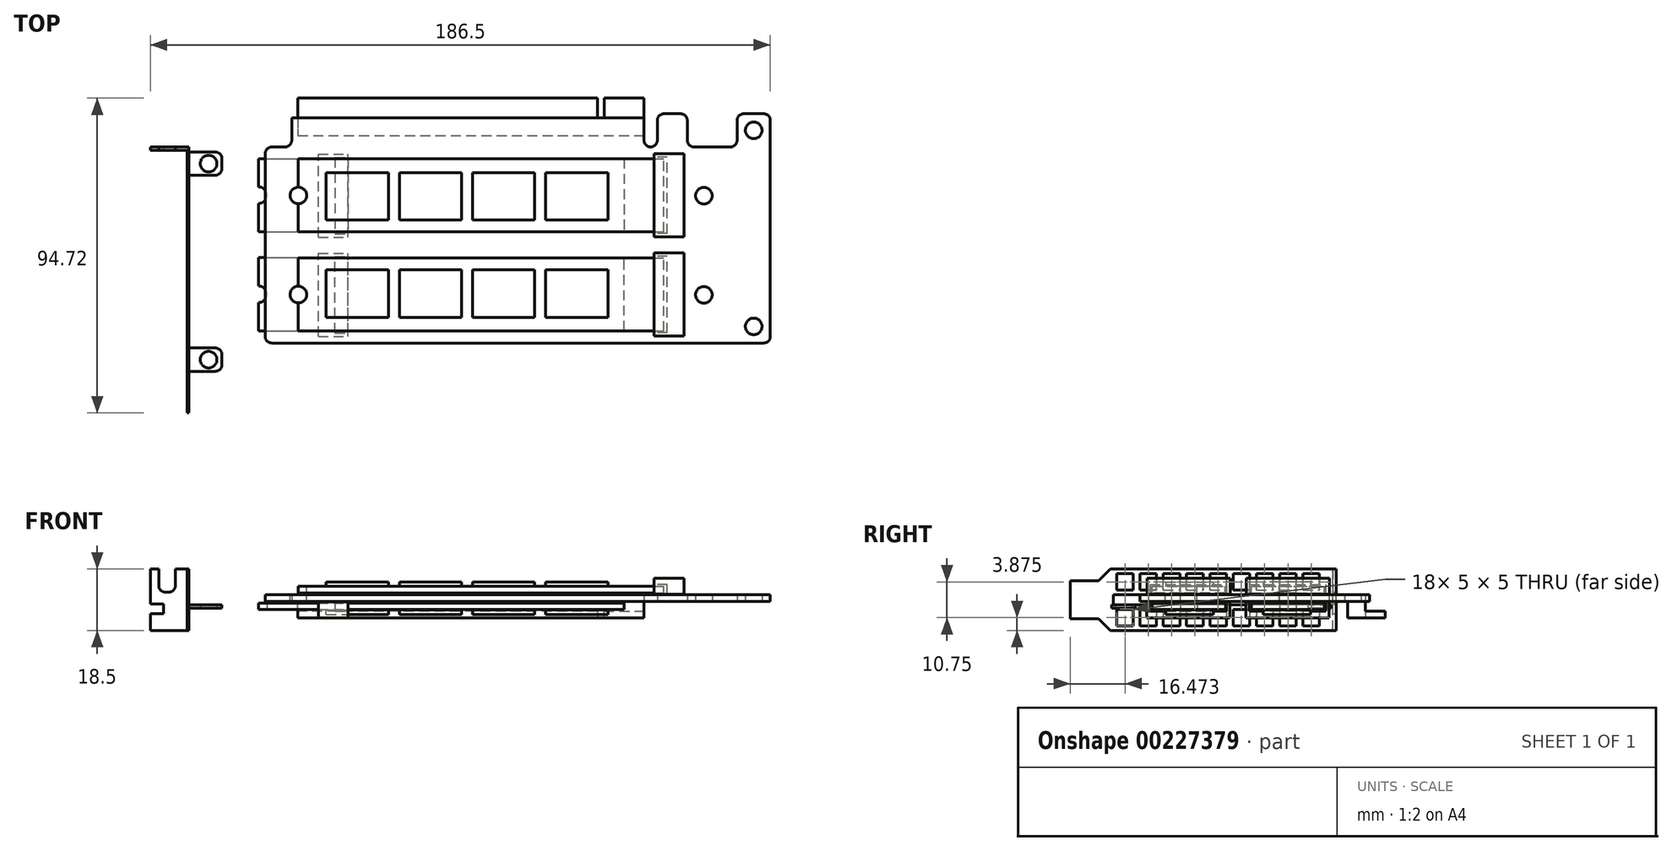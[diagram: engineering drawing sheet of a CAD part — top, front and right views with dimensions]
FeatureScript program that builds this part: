
annotation { "Feature Type Name" : "Feature", "Feature Type Description" : "" }
export const myFeature = defineFeature(function(context is Context, id is Id, definition is map)
    precondition{}
    {
        {
            var Q0;
            Q0=qCreatedBy(makeId("Top.planeOp"),FACE);
            var sketch = newSketch(context, id + "F0", { "sketchPlane" : qUnion([Q0])});
            skLineSegment(sketch, "E0.top", {"start": v(76, 34.5) * mm, "end": v(-76, 34.5) * mm});
            skLineSegment(sketch, "E0.right", {"start": v(-76, -34.5) * mm, "end": v(-76, 34.5) * mm});
            skPoint(sketch, "E0.middle", {"position": v(0, 0) * mm});
            skLineSegment(sketch, "E1", {"start": v(-76, -34.5) * mm, "end": v(-66, -34.5) * mm});
            skLineSegment(sketch, "E2", {"start": v(-66, -34.5) * mm, "end": v(-66, -24.5) * mm});
            skLineSegment(sketch, "E3", {"start": v(-66, -24.5) * mm, "end": v(-51, -24.5) * mm});
            skLineSegment(sketch, "E4", {"start": v(-51, -24.5) * mm, "end": v(-51, -34.5) * mm});
            skLineSegment(sketch, "E5", {"start": v(-51, -34.5) * mm, "end": v(-42, -34.5) * mm});
            skLineSegment(sketch, "E6", {"start": v(-42, -34.5) * mm, "end": v(-42, -24.5) * mm});
            skLineSegment(sketch, "E7", {"start": v(-42, -24.5) * mm, "end": v(-38, -24.5) * mm});
            skLineSegment(sketch, "E8", {"start": v(-38, -24.5) * mm, "end": v(-38, -39.95) * mm});
            skLineSegment(sketch, "E9", {"start": v(-38, -39.95) * mm, "end": v(-26, -39.95) * mm});
            skLineSegment(sketch, "E10", {"start": v(-26, -39.95) * mm, "end": v(-26, -29.95) * mm});
            skLineSegment(sketch, "E11", {"start": v(-26, -29.95) * mm, "end": v(-24, -29.95) * mm});
            skLineSegment(sketch, "E12", {"start": v(-24, -29.95) * mm, "end": v(-24, -39.95) * mm});
            skLineSegment(sketch, "E13", {"start": v(-24, -39.95) * mm, "end": v(68, -39.95) * mm});
            skLineSegment(sketch, "E14", {"start": v(68, -39.95) * mm, "end": v(68, -24.5) * mm});
            skLineSegment(sketch, "E15", {"start": v(76, 34.5) * mm, "end": v(76, -24.5) * mm});
            skLineSegment(sketch, "E16", {"start": v(-76, -34.5) * mm, "end": v(-66, -24.5) * mm, "construction": true});
            skCircle(sketch, "E17", {"center": v(-71, -29.5) * mm, "radius": 2.5 * mm});
            skLineSegment(sketch, "E18", {"start": v(-76, 0) * mm, "end": v(0, 0) * mm, "construction": true});
            skCircle(sketch, "E19.MirrorC", {"center": v(-71, 29.5) * mm, "radius": 2.5 * mm});
            skLineSegment(sketch, "E20", {"start": v(68, -24.5) * mm, "end": v(76, -24.5) * mm});
            skSolve(sketch);
        }
        {
            var Q0;
            Q0 = qSketchRegion(id + "F0", true);
            extrude(context, id + "F1", {"entities" : qUnion([Q0]), "depth" : 2 * mm});
        }
        {
            var Q0;
            Q0=makeQuery(id+"F1.opExtrude","CAP_FACE",FACE,{"disambiguationData":[OSD([sQuery(id+"F0.wireOp",EDGE,"E0.top"),sQuery(id+"F0.wireOp",EDGE,"E0.right"),sQuery(id+"F0.wireOp",EDGE,"E1"),sQuery(id+"F0.wireOp",EDGE,"E2"),sQuery(id+"F0.wireOp",EDGE,"E3"),sQuery(id+"F0.wireOp",EDGE,"E4"),sQuery(id+"F0.wireOp",EDGE,"E5"),sQuery(id+"F0.wireOp",EDGE,"E6"),sQuery(id+"F0.wireOp",EDGE,"E7"),sQuery(id+"F0.wireOp",EDGE,"E8"),sQuery(id+"F0.wireOp",EDGE,"E9"),sQuery(id+"F0.wireOp",EDGE,"E10"),sQuery(id+"F0.wireOp",EDGE,"E11"),sQuery(id+"F0.wireOp",EDGE,"E12"),sQuery(id+"F0.wireOp",EDGE,"E13"),sQuery(id+"F0.wireOp",EDGE,"E14"),sQuery(id+"F0.wireOp",EDGE,"E15"),sQuery(id+"F0.wireOp",EDGE,"E17"),sQuery(id+"F0.wireOp",EDGE,"E19.MirrorC"),sQuery(id+"F0.wireOp",EDGE,"E20")])],"isStart":false});
            var sketch = newSketch(context, id + "F2", { "sketchPlane" : qUnion([Q0])});
            skLineSegment(sketch, "E21.bottom", {"start": v(-50, 2.58) * mm, "end": v(-41, 2.58) * mm});
            skLineSegment(sketch, "E21.top", {"start": v(-50, -22.42) * mm, "end": v(-41, -22.42) * mm});
            skLineSegment(sketch, "E21.left", {"start": v(-50, 2.58) * mm, "end": v(-50, -22.42) * mm});
            skLineSegment(sketch, "E21.right", {"start": v(-41, 2.58) * mm, "end": v(-41, -22.42) * mm});
            skLineSegment(sketch, "E22", {"start": v(-66, -24.5) * mm, "end": v(-66, 34.5) * mm, "construction": true});
            skLineSegment(sketch, "E23", {"start": v(-66, 5) * mm, "end": v(-44.12, 5) * mm, "construction": true});
            skLineSegment(sketch, "E24.MirrorCS", {"start": v(-41, 7.42) * mm, "end": v(-41, 32.42) * mm});
            skLineSegment(sketch, "E25.MirrorCS", {"start": v(-50, 7.42) * mm, "end": v(-41, 7.42) * mm});
            skLineSegment(sketch, "E26.MirrorCS", {"start": v(-50, 7.42) * mm, "end": v(-50, 32.42) * mm});
            skLineSegment(sketch, "E27.MirrorCS", {"start": v(-50, 32.42) * mm, "end": v(-41, 32.42) * mm});
            skLineSegment(sketch, "E28", {"start": v(-50, 32.42) * mm, "end": v(-66, 32.42) * mm, "construction": true});
            skLineSegment(sketch, "E29.bottom", {"start": v(-36.45, -34.95) * mm, "end": v(-27.66, -34.95) * mm});
            skLineSegment(sketch, "E29.top", {"start": v(-36.45, -39.95) * mm, "end": v(-27.66, -39.95) * mm});
            skLineSegment(sketch, "E29.left", {"start": v(-36.45, -34.95) * mm, "end": v(-36.45, -39.95) * mm});
            skLineSegment(sketch, "E29.right", {"start": v(-27.66, -34.95) * mm, "end": v(-27.66, -39.95) * mm});
            skLineSegment(sketch, "E30.bottom", {"start": v(-22.05, -34.95) * mm, "end": v(65.79, -34.95) * mm});
            skLineSegment(sketch, "E30.top", {"start": v(-22.05, -39.95) * mm, "end": v(65.79, -39.95) * mm});
            skLineSegment(sketch, "E30.left", {"start": v(-22.05, -34.95) * mm, "end": v(-22.05, -39.95) * mm});
            skLineSegment(sketch, "E30.right", {"start": v(65.79, -34.95) * mm, "end": v(65.79, -39.95) * mm});
            skSolve(sketch);
        }
        {
            var Q0;
            Q0=makeQuery(id+"F2.imprint","IMPRINT",FACE,{"disambiguationData":[TD([[makeQuery(id+"F2.imprint","IMPRINT",EDGE,{"derivedFrom":sQuery(id+"F2.wireOp",EDGE,"E21.bottom")}),-1.0]])]});
            var Q1;
            Q1=makeQuery(id+"F2.imprint","IMPRINT",FACE,{"disambiguationData":[TD([[makeQuery(id+"F2.imprint","IMPRINT",EDGE,{"derivedFrom":sQuery(id+"F2.wireOp",EDGE,"E24.MirrorCS")}),1.0]])]});
            extrude(context, id + "F3", {"entities" : qUnion([Q0, Q1]), "operationType" : NewBodyOperationType.ADD, "depth" : 5 * mm});
        }
        {
            var Q0;
            Q0=makeQuery(id+"F3.opExtrude","SWEPT_FACE",FACE,{"disambiguationData":[OSD([sQuery(id+"F2.wireOp",EDGE,"E24.MirrorCS")])]});
            var sketch = newSketch(context, id + "F4", { "sketchPlane" : qUnion([Q0])});
            skLineSegment(sketch, "E31.bottom", {"start": v(31.42, 2) * mm, "end": v(8.42, 2) * mm});
            skLineSegment(sketch, "E31.top", {"start": v(31.42, 5) * mm, "end": v(8.42, 5) * mm});
            skLineSegment(sketch, "E31.left", {"start": v(31.42, 2) * mm, "end": v(31.42, 5) * mm});
            skLineSegment(sketch, "E31.right", {"start": v(8.42, 2) * mm, "end": v(8.42, 5) * mm});
            skLineSegment(sketch, "E32", {"start": v(31.42, 3.5) * mm, "end": v(32.42, 3.5) * mm, "construction": true});
            skSolve(sketch);
        }
        {
            var Q0;
            Q0 = qSketchRegion(id + "F4", true);
            extrude(context, id + "F5", {"entities" : qUnion([Q0]), "operationType" : NewBodyOperationType.REMOVE, "oppositeDirection" : true, "depth" : 4 * mm});
        }
        {
            var Q0;
            Q0=makeQuery(id+"F3.opExtrude","SWEPT_FACE",FACE,{"disambiguationData":[OSD([sQuery(id+"F2.wireOp",EDGE,"E21.right")])]});
            var sketch = newSketch(context, id + "F6", { "sketchPlane" : qUnion([Q0])});
            skLineSegment(sketch, "E33.0", {"start": v(31.42, 5) * mm, "end": v(8.42, 5) * mm, "construction": true});
            skLineSegment(sketch, "E34.0", {"start": v(8.42, 2) * mm, "end": v(8.42, 5) * mm, "construction": true});
            skLineSegment(sketch, "E35", {"start": v(2.58, 4.5) * mm, "end": v(1.58, 4.5) * mm, "construction": true});
            skLineSegment(sketch, "E36.bottom", {"start": v(1.58, 2) * mm, "end": v(-21.42, 2) * mm});
            skLineSegment(sketch, "E36.top", {"start": v(1.58, 5) * mm, "end": v(-21.42, 5) * mm});
            skLineSegment(sketch, "E36.left", {"start": v(1.58, 2) * mm, "end": v(1.58, 5) * mm});
            skLineSegment(sketch, "E36.right", {"start": v(-21.42, 2) * mm, "end": v(-21.42, 5) * mm});
            skSolve(sketch);
        }
        {
            var Q0;
            Q0 = qSketchRegion(id + "F6", true);
            extrude(context, id + "F7", {"entities" : qUnion([Q0]), "operationType" : NewBodyOperationType.REMOVE, "oppositeDirection" : true, "depth" : 4 * mm});
        }
        {
            var Q0;
            Q0=makeQuery(id+"F7.boolean.opBoolean","COPY",FACE,{"derivedFrom":makeQuery(id+"F7.opExtrude","CAP_FACE",FACE,{"disambiguationData":[OSD([sQuery(id+"F6.wireOp",EDGE,"E36.bottom"),sQuery(id+"F6.wireOp",EDGE,"E36.top"),sQuery(id+"F6.wireOp",EDGE,"E36.left"),sQuery(id+"F6.wireOp",EDGE,"E36.right")])],"isStart":false})});
            cPlane(context, id + "F8", {"entities" : qUnion([Q0]), "cplaneType" : CPlaneType.OFFSET, "offset" : 1 * mm, "width" : 150 * mm, "height" : 150 * mm});
        }
        {
            var Q0;
            Q0=qCreatedBy(id+"F8.planeOp",FACE);
            var sketch = newSketch(context, id + "F9", { "sketchPlane" : qUnion([Q0])});
            skLineSegment(sketch, "E37.0", {"start": v(1.58, 5) * mm, "end": v(-21.42, 5) * mm, "construction": true});
            skLineSegment(sketch, "E37.1", {"start": v(1.58, 2) * mm, "end": v(1.58, 5) * mm, "construction": true});
            skLineSegment(sketch, "E37.2", {"start": v(-21.42, 2) * mm, "end": v(-21.42, 5) * mm, "construction": true});
            skLineSegment(sketch, "E37.3", {"start": v(8.42, 2) * mm, "end": v(31.42, 2) * mm, "construction": true});
            skLineSegment(sketch, "E37.4", {"start": v(8.42, 2) * mm, "end": v(8.42, 5) * mm, "construction": true});
            skLineSegment(sketch, "E37.5", {"start": v(31.42, 2) * mm, "end": v(31.42, 5) * mm, "construction": true});
            skLineSegment(sketch, "E37.6", {"start": v(31.42, 5) * mm, "end": v(8.42, 5) * mm, "construction": true});
            skLineSegment(sketch, "E37.7", {"start": v(1.58, 2) * mm, "end": v(-21.42, 2) * mm, "construction": true});
            skPoint(sketch, "E37.8", {"position": v(8.42, 3.5) * mm});
            skLineSegment(sketch, "E38.0", {"start": v(8.92, 2.5) * mm, "end": v(30.92, 2.5) * mm});
            skLineSegment(sketch, "E38.1", {"start": v(8.92, 2.5) * mm, "end": v(8.92, 4.5) * mm});
            skLineSegment(sketch, "E38.2", {"start": v(30.92, 4.5) * mm, "end": v(8.92, 4.5) * mm});
            skLineSegment(sketch, "E38.3", {"start": v(30.92, 2.5) * mm, "end": v(30.92, 4.5) * mm});
            skLineSegment(sketch, "E39.0", {"start": v(1.08, 4.5) * mm, "end": v(-20.92, 4.5) * mm});
            skLineSegment(sketch, "E39.1", {"start": v(1.08, 2.5) * mm, "end": v(1.08, 4.5) * mm});
            skLineSegment(sketch, "E39.2", {"start": v(1.08, 2.5) * mm, "end": v(-20.92, 2.5) * mm});
            skLineSegment(sketch, "E39.3", {"start": v(-20.92, 2.5) * mm, "end": v(-20.92, 4.5) * mm});
            skSolve(sketch);
        }
        {
            var Q0;
            Q0 = qSketchRegion(id + "F9", true);
            extrude(context, id + "F10", {"entities" : qUnion([Q0]), "depth" : 110 * mm});
        }
        {
            var Q0;
            Q0=makeQuery(id+"F1.opExtrude","CAP_FACE",FACE,{"disambiguationData":[OSD([sQuery(id+"F0.wireOp",EDGE,"E0.top"),sQuery(id+"F0.wireOp",EDGE,"E0.right"),sQuery(id+"F0.wireOp",EDGE,"E1"),sQuery(id+"F0.wireOp",EDGE,"E2"),sQuery(id+"F0.wireOp",EDGE,"E3"),sQuery(id+"F0.wireOp",EDGE,"E4"),sQuery(id+"F0.wireOp",EDGE,"E5"),sQuery(id+"F0.wireOp",EDGE,"E6"),sQuery(id+"F0.wireOp",EDGE,"E7"),sQuery(id+"F0.wireOp",EDGE,"E8"),sQuery(id+"F0.wireOp",EDGE,"E9"),sQuery(id+"F0.wireOp",EDGE,"E10"),sQuery(id+"F0.wireOp",EDGE,"E11"),sQuery(id+"F0.wireOp",EDGE,"E12"),sQuery(id+"F0.wireOp",EDGE,"E13"),sQuery(id+"F0.wireOp",EDGE,"E14"),sQuery(id+"F0.wireOp",EDGE,"E15"),sQuery(id+"F0.wireOp",EDGE,"E17"),sQuery(id+"F0.wireOp",EDGE,"E19.MirrorC"),sQuery(id+"F0.wireOp",EDGE,"E20")])],"isStart":true});
            var sketch = newSketch(context, id + "F11", { "sketchPlane" : qUnion([Q0])});
            skLineSegment(sketch, "E40", {"start": v(60, -34.5) * mm, "end": v(60, -32.5) * mm, "construction": true});
            skLineSegment(sketch, "E41", {"start": v(60, -32.5) * mm, "end": v(76, -32.5) * mm, "construction": true});
            skLineSegment(sketch, "E42.bottom", {"start": v(60, -32.5) * mm, "end": v(51, -32.5) * mm});
            skLineSegment(sketch, "E42.top", {"start": v(60, -7.5) * mm, "end": v(51, -7.5) * mm});
            skLineSegment(sketch, "E42.left", {"start": v(60, -32.5) * mm, "end": v(60, -7.5) * mm});
            skLineSegment(sketch, "E42.right", {"start": v(51, -32.5) * mm, "end": v(51, -7.5) * mm});
            skLineSegment(sketch, "E43", {"start": v(60, -7.5) * mm, "end": v(60, -2.67) * mm, "construction": true});
            skLineSegment(sketch, "E44.bottom", {"start": v(60, -2.67) * mm, "end": v(51, -2.67) * mm});
            skLineSegment(sketch, "E44.top", {"start": v(60, 22.33) * mm, "end": v(51, 22.33) * mm});
            skLineSegment(sketch, "E44.left", {"start": v(60, -2.67) * mm, "end": v(60, 22.33) * mm});
            skLineSegment(sketch, "E44.right", {"start": v(51, -2.67) * mm, "end": v(51, 22.33) * mm});
            skPoint(sketch, "E45.0", {"position": v(65.79, 37.45) * mm});
            skLineSegment(sketch, "E46.0", {"start": v(65.79, 34.95) * mm, "end": v(65.79, 39.95) * mm});
            skLineSegment(sketch, "E47.0", {"start": v(-22.05, 34.95) * mm, "end": v(65.79, 34.95) * mm});
            skLineSegment(sketch, "E48.0", {"start": v(-22.05, 39.95) * mm, "end": v(65.79, 39.95) * mm});
            skPoint(sketch, "E49.0", {"position": v(-22.05, 37.45) * mm});
            skLineSegment(sketch, "E50.0", {"start": v(-22.05, 34.95) * mm, "end": v(-22.05, 39.95) * mm});
            skLineSegment(sketch, "E51.0", {"start": v(-27.66, 34.95) * mm, "end": v(-27.66, 39.95) * mm});
            skLineSegment(sketch, "E52.0", {"start": v(-36.45, 34.95) * mm, "end": v(-27.66, 34.95) * mm});
            skLineSegment(sketch, "E53.0", {"start": v(-36.45, 34.95) * mm, "end": v(-36.45, 39.95) * mm});
            skLineSegment(sketch, "E54.0", {"start": v(-36.45, 39.95) * mm, "end": v(-27.66, 39.95) * mm});
            skSolve(sketch);
        }
        {
            var Q0;
            Q0=makeQuery(id+"F11.imprint","IMPRINT",FACE,{"disambiguationData":[TD([[makeQuery(id+"F11.imprint","IMPRINT",EDGE,{"derivedFrom":sQuery(id+"F11.wireOp",EDGE,"E42.bottom")}),-1.0]])]});
            var Q1;
            Q1=makeQuery(id+"F11.imprint","IMPRINT",FACE,{"disambiguationData":[TD([[makeQuery(id+"F11.imprint","IMPRINT",EDGE,{"derivedFrom":sQuery(id+"F11.wireOp",EDGE,"E44.bottom")}),-1.0]])]});
            extrude(context, id + "F12", {"entities" : qUnion([Q0, Q1]), "operationType" : NewBodyOperationType.ADD, "depth" : 5 * mm});
        }
        {
            var Q0;
            Q0=makeQuery(id+"F12.opExtrude","SWEPT_FACE",FACE,{"disambiguationData":[OSD([sQuery(id+"F11.wireOp",EDGE,"E42.right")])]});
            var sketch = newSketch(context, id + "F13", { "sketchPlane" : qUnion([Q0])});
            skPoint(sketch, "E55.0", {"position": v(-2.67, -5) * mm});
            skLineSegment(sketch, "E56", {"start": v(-7.5, -5) * mm, "end": v(-2.67, -5) * mm, "construction": true});
            skLineSegment(sketch, "E57", {"start": v(-5.09, -5) * mm, "end": v(-5.09, 0) * mm, "construction": true});
            skLineSegment(sketch, "E58.bottom", {"start": v(-31.5, 0) * mm, "end": v(-8.5, 0) * mm});
            skLineSegment(sketch, "E58.top", {"start": v(-31.5, -3) * mm, "end": v(-8.5, -3) * mm});
            skLineSegment(sketch, "E58.left", {"start": v(-31.5, 0) * mm, "end": v(-31.5, -3) * mm});
            skLineSegment(sketch, "E58.right", {"start": v(-8.5, 0) * mm, "end": v(-8.5, -3) * mm});
            skLineSegment(sketch, "E59", {"start": v(-31.5, -1.5) * mm, "end": v(-32.5, -1.5) * mm, "construction": true});
            skLineSegment(sketch, "E60", {"start": v(-8.5, -1.5) * mm, "end": v(-7.5, -1.5) * mm, "construction": true});
            skLineSegment(sketch, "E61.MirrorCS", {"start": v(-1.67, 0) * mm, "end": v(-1.67, -3) * mm});
            skLineSegment(sketch, "E62.MirrorCS", {"start": v(21.33, -3) * mm, "end": v(-1.67, -3) * mm});
            skLineSegment(sketch, "E63.MirrorCS", {"start": v(21.33, 0) * mm, "end": v(-1.67, 0) * mm});
            skLineSegment(sketch, "E64.MirrorCS", {"start": v(21.33, 0) * mm, "end": v(21.33, -3) * mm});
            skSolve(sketch);
        }
        {
            var Q0;
            Q0 = qSketchRegion(id + "F13", true);
            extrude(context, id + "F14", {"entities" : qUnion([Q0]), "operationType" : NewBodyOperationType.REMOVE, "oppositeDirection" : true, "depth" : 4 * mm});
        }
        {
            var Q0;
            Q0=makeQuery(id+"F14.boolean.opBoolean","COPY",FACE,{"derivedFrom":makeQuery(id+"F14.opExtrude","CAP_FACE",FACE,{"disambiguationData":[OSD([sQuery(id+"F13.wireOp",EDGE,"E58.bottom"),sQuery(id+"F13.wireOp",EDGE,"E58.top"),sQuery(id+"F13.wireOp",EDGE,"E58.left"),sQuery(id+"F13.wireOp",EDGE,"E58.right")])],"isStart":false})});
            cPlane(context, id + "F15", {"entities" : qUnion([Q0]), "cplaneType" : CPlaneType.OFFSET, "offset" : 1 * mm, "width" : 150 * mm, "height" : 150 * mm});
        }
        {
            var Q0;
            Q0=qCreatedBy(id+"F15.planeOp",FACE);
            var sketch = newSketch(context, id + "F16", { "sketchPlane" : qUnion([Q0])});
            skLineSegment(sketch, "E65.0.0", {"start": v(-8.5, -3) * mm, "end": v(-8.5, 0) * mm, "construction": true});
            skLineSegment(sketch, "E65.0.1", {"start": v(-8.5, 0) * mm, "end": v(-31.5, 0) * mm, "construction": true});
            skLineSegment(sketch, "E65.0.2", {"start": v(-31.5, 0) * mm, "end": v(-31.5, -3) * mm, "construction": true});
            skLineSegment(sketch, "E65.0.3", {"start": v(-31.5, -3) * mm, "end": v(-8.5, -3) * mm, "construction": true});
            skLineSegment(sketch, "E66.0", {"start": v(-31, -2.5) * mm, "end": v(-9, -2.5) * mm});
            skLineSegment(sketch, "E66.1", {"start": v(-31, -0.5) * mm, "end": v(-31, -2.5) * mm});
            skLineSegment(sketch, "E66.2", {"start": v(-9, -0.5) * mm, "end": v(-31, -0.5) * mm});
            skLineSegment(sketch, "E66.3", {"start": v(-9, -2.5) * mm, "end": v(-9, -0.5) * mm});
            skLineSegment(sketch, "E67.0", {"start": v(-5.09, -5) * mm, "end": v(-5.09, 0) * mm, "construction": true});
            skLineSegment(sketch, "E68.MirrorCS", {"start": v(-1.17, -2.5) * mm, "end": v(-1.17, -0.5) * mm});
            skLineSegment(sketch, "E69.MirrorCS", {"start": v(20.83, -2.5) * mm, "end": v(-1.17, -2.5) * mm});
            skLineSegment(sketch, "E70.MirrorCS", {"start": v(-1.17, -0.5) * mm, "end": v(20.83, -0.5) * mm});
            skLineSegment(sketch, "E71.MirrorCS", {"start": v(20.83, -0.5) * mm, "end": v(20.83, -2.5) * mm});
            skSolve(sketch);
        }
        {
            var Q0;
            Q0 = qSketchRegion(id + "F16", true);
            extrude(context, id + "F17", {"entities" : qUnion([Q0]), "depth" : 110 * mm});
        }
        {
            var Q0;
            Q0=makeQuery(id+"F17.opExtrude","SWEPT_FACE",FACE,{"disambiguationData":[OSD([sQuery(id+"F16.wireOp",EDGE,"E66.0")])]});
            var sketch = newSketch(context, id + "F18", { "sketchPlane" : qUnion([Q0])});
            skPoint(sketch, "E72.0", {"position": v(-56, -20) * mm});
            skPoint(sketch, "E73.0", {"position": v(-56, 9.83) * mm});
            skCircle(sketch, "E74", {"center": v(-56, -20) * mm, "radius": 2.5 * mm});
            skCircle(sketch, "E75", {"center": v(-56, 9.83) * mm, "radius": 2.5 * mm});
            skSolve(sketch);
        }
        {
            var Q0;
            Q0 = qSketchRegion(id + "F18", true);
            extrude(context, id + "F19", {"entities" : qUnion([Q0]), "operationType" : NewBodyOperationType.REMOVE, "oppositeDirection" : true, "depth" : 5 * mm});
        }
        {
            var Q0;
            Q0=makeQuery(id+"F1.opExtrude","SWEPT_EDGE",EDGE,{"disambiguationData":[OSD([sQuery(id+"F0.wireOp",EDGE,"E14"),sQuery(id+"F0.wireOp",EDGE,"E20")])]});
            var Q1;
            Q1=makeQuery(id+"F1.opExtrude","SWEPT_EDGE",EDGE,{"disambiguationData":[OSD([sQuery(id+"F0.wireOp",EDGE,"E6"),sQuery(id+"F0.wireOp",EDGE,"E7")])]});
            var Q2;
            Q2=makeQuery(id+"F1.opExtrude","SWEPT_EDGE",EDGE,{"disambiguationData":[OSD([sQuery(id+"F0.wireOp",EDGE,"E7"),sQuery(id+"F0.wireOp",EDGE,"E8")])]});
            var Q3;
            Q3=makeQuery(id+"F1.opExtrude","SWEPT_EDGE",EDGE,{"disambiguationData":[OSD([sQuery(id+"F0.wireOp",EDGE,"E5"),sQuery(id+"F0.wireOp",EDGE,"E6")])]});
            var Q4;
            Q4=makeQuery(id+"F1.opExtrude","SWEPT_EDGE",EDGE,{"disambiguationData":[OSD([sQuery(id+"F0.wireOp",EDGE,"E4"),sQuery(id+"F0.wireOp",EDGE,"E5")])]});
            var Q5;
            Q5=makeQuery(id+"F1.opExtrude","SWEPT_EDGE",EDGE,{"disambiguationData":[OSD([sQuery(id+"F0.wireOp",EDGE,"E3"),sQuery(id+"F0.wireOp",EDGE,"E4")])]});
            var Q6;
            Q6=makeQuery(id+"F1.opExtrude","SWEPT_EDGE",EDGE,{"disambiguationData":[OSD([sQuery(id+"F0.wireOp",EDGE,"E2"),sQuery(id+"F0.wireOp",EDGE,"E3")])]});
            var Q7;
            Q7=makeQuery(id+"F1.opExtrude","SWEPT_EDGE",EDGE,{"disambiguationData":[OSD([sQuery(id+"F0.wireOp",EDGE,"E1"),sQuery(id+"F0.wireOp",EDGE,"E2")])]});
            var Q8;
            Q8=makeQuery(id+"F1.opExtrude","SWEPT_EDGE",EDGE,{"disambiguationData":[OSD([sQuery(id+"F0.wireOp",EDGE,"E0.right"),sQuery(id+"F0.wireOp",EDGE,"E1")])]});
            var Q9;
            Q9=makeQuery(id+"F1.opExtrude","SWEPT_EDGE",EDGE,{"disambiguationData":[OSD([sQuery(id+"F0.wireOp",EDGE,"E0.top"),sQuery(id+"F0.wireOp",EDGE,"E0.right")])]});
            fillet(context, id + "F20", {"entities" : qUnion([Q0, Q1, Q2, Q3, Q4, Q5, Q6, Q7, Q8, Q9]), "radius" : 2 * mm, "tangentPropagation" : true, "allowEdgeOverflow" : false});
        }
        {
            var Q0;
            Q0=makeQuery(id+"F14.boolean.opBoolean","MERGE",FACE,{"derivedFrom":[makeQuery(id+"F1.opExtrude","CAP_FACE",FACE,{"disambiguationData":[OSD([sQuery(id+"F0.wireOp",EDGE,"E0.top"),sQuery(id+"F0.wireOp",EDGE,"E0.right"),sQuery(id+"F0.wireOp",EDGE,"E1"),sQuery(id+"F0.wireOp",EDGE,"E2"),sQuery(id+"F0.wireOp",EDGE,"E3"),sQuery(id+"F0.wireOp",EDGE,"E4"),sQuery(id+"F0.wireOp",EDGE,"E5"),sQuery(id+"F0.wireOp",EDGE,"E6"),sQuery(id+"F0.wireOp",EDGE,"E7"),sQuery(id+"F0.wireOp",EDGE,"E8"),sQuery(id+"F0.wireOp",EDGE,"E9"),sQuery(id+"F0.wireOp",EDGE,"E10"),sQuery(id+"F0.wireOp",EDGE,"E11"),sQuery(id+"F0.wireOp",EDGE,"E12"),sQuery(id+"F0.wireOp",EDGE,"E13"),sQuery(id+"F0.wireOp",EDGE,"E14"),sQuery(id+"F0.wireOp",EDGE,"E15"),sQuery(id+"F0.wireOp",EDGE,"E17"),sQuery(id+"F0.wireOp",EDGE,"E19.MirrorC"),sQuery(id+"F0.wireOp",EDGE,"E20")])],"isStart":true}),makeQuery(id+"F14.opExtrude","SWEPT_FACE",FACE,{"disambiguationData":[OSD([sQuery(id+"F13.wireOp",EDGE,"E58.bottom")])]}),makeQuery(id+"F14.opExtrude","SWEPT_FACE",FACE,{"disambiguationData":[OSD([sQuery(id+"F13.wireOp",EDGE,"E63.MirrorCS")])]})]});
            var sketch = newSketch(context, id + "F21", { "sketchPlane" : qUnion([Q0])});
            skLineSegment(sketch, "E76.bottom", {"start": v(68, 39.95) * mm, "end": v(-38, 39.95) * mm});
            skLineSegment(sketch, "E76.top", {"start": v(68, 33.22) * mm, "end": v(-38, 33.22) * mm});
            skLineSegment(sketch, "E76.left", {"start": v(68, 39.95) * mm, "end": v(68, 33.22) * mm});
            skLineSegment(sketch, "E76.right", {"start": v(-38, 39.95) * mm, "end": v(-38, 33.22) * mm});
            skSolve(sketch);
        }
        {
            var Q0;
            Q0 = qSketchRegion(id + "F21", true);
            extrude(context, id + "F22", {"entities" : qUnion([Q0]), "operationType" : NewBodyOperationType.REMOVE, "endBound" : BoundingType.THROUGH_ALL, "oppositeDirection" : true, "depth" : 25 * mm});
        }
        {
            var Q0;
            Q0=makeQuery(id+"F14.boolean.opBoolean","MERGE",FACE,{"derivedFrom":[makeQuery(id+"F1.opExtrude","CAP_FACE",FACE,{"disambiguationData":[OSD([sQuery(id+"F0.wireOp",EDGE,"E0.top"),sQuery(id+"F0.wireOp",EDGE,"E0.right"),sQuery(id+"F0.wireOp",EDGE,"E1"),sQuery(id+"F0.wireOp",EDGE,"E2"),sQuery(id+"F0.wireOp",EDGE,"E3"),sQuery(id+"F0.wireOp",EDGE,"E4"),sQuery(id+"F0.wireOp",EDGE,"E5"),sQuery(id+"F0.wireOp",EDGE,"E6"),sQuery(id+"F0.wireOp",EDGE,"E7"),sQuery(id+"F0.wireOp",EDGE,"E8"),sQuery(id+"F0.wireOp",EDGE,"E9"),sQuery(id+"F0.wireOp",EDGE,"E10"),sQuery(id+"F0.wireOp",EDGE,"E11"),sQuery(id+"F0.wireOp",EDGE,"E12"),sQuery(id+"F0.wireOp",EDGE,"E13"),sQuery(id+"F0.wireOp",EDGE,"E14"),sQuery(id+"F0.wireOp",EDGE,"E15"),sQuery(id+"F0.wireOp",EDGE,"E17"),sQuery(id+"F0.wireOp",EDGE,"E19.MirrorC"),sQuery(id+"F0.wireOp",EDGE,"E20")])],"isStart":true}),makeQuery(id+"F14.opExtrude","SWEPT_FACE",FACE,{"disambiguationData":[OSD([sQuery(id+"F13.wireOp",EDGE,"E58.bottom")])]}),makeQuery(id+"F14.opExtrude","SWEPT_FACE",FACE,{"disambiguationData":[OSD([sQuery(id+"F13.wireOp",EDGE,"E63.MirrorCS")])]})]});
            var sketch = newSketch(context, id + "F23", { "sketchPlane" : qUnion([Q0])});
            skLineSegment(sketch, "E77.bottom", {"start": v(66.12, 33.22) * mm, "end": v(-38, 33.22) * mm});
            skLineSegment(sketch, "E77.top", {"start": v(66.12, 27.97) * mm, "end": v(-38, 27.97) * mm});
            skLineSegment(sketch, "E77.left", {"start": v(66.12, 33.22) * mm, "end": v(66.12, 27.97) * mm});
            skLineSegment(sketch, "E77.right", {"start": v(-38, 33.22) * mm, "end": v(-38, 27.97) * mm});
            skSolve(sketch);
        }
        {
            var Q0;
            Q0 = qSketchRegion(id + "F23", true);
            extrude(context, id + "F24", {"entities" : qUnion([Q0]), "operationType" : NewBodyOperationType.ADD, "depth" : 5 * mm});
        }
        {
            var Q0;
            {var subQ7=sQuery(id+"F0.wireOp",EDGE,"E12");var subQ10=sQuery(id+"F0.wireOp",EDGE,"E8");var subQ26=makeQuery(id+"F22.opExtrude","SWEPT_FACE",FACE,{"disambiguationData":[OSD([sQuery(id+"F21.wireOp",EDGE,"E76.top")])]});Q0=makeQuery(id+"F24.boolean.opBoolean","MERGE",FACE,{"derivedFrom":[makeQuery(id+"F22.boolean.opBoolean","COPY",FACE,{"disambiguationData":[TD([makeQuery(id+"F1.opExtrude","SWEPT_FACE",FACE,{"disambiguationData":[OSD([subQ7])]})])],"derivedFrom":subQ26}),makeQuery(id+"F22.boolean.opBoolean","COPY",FACE,{"disambiguationData":[TD([makeQuery(id+"F1.opExtrude","SWEPT_FACE",FACE,{"disambiguationData":[OSD([subQ10])]})])],"derivedFrom":subQ26}),makeQuery(id+"F24.opExtrude","SWEPT_FACE",FACE,{"disambiguationData":[OSD([sQuery(id+"F23.wireOp",EDGE,"E77.bottom")])]})]});}
            var sketch = newSketch(context, id + "F25", { "sketchPlane" : qUnion([Q0])});
            skLineSegment(sketch, "E78.bottom", {"start": v(-26, -5) * mm, "end": v(-38, -5) * mm});
            skLineSegment(sketch, "E78.top", {"start": v(-26, -3) * mm, "end": v(-38, -3) * mm});
            skLineSegment(sketch, "E78.left", {"start": v(-26, -5) * mm, "end": v(-26, -3) * mm});
            skLineSegment(sketch, "E78.right", {"start": v(-38, -5) * mm, "end": v(-38, -3) * mm});
            skLineSegment(sketch, "E79.bottom", {"start": v(-24, -3) * mm, "end": v(66.12, -3) * mm});
            skLineSegment(sketch, "E79.top", {"start": v(-24, -5) * mm, "end": v(66.12, -5) * mm});
            skLineSegment(sketch, "E79.left", {"start": v(-24, -3) * mm, "end": v(-24, -5) * mm});
            skLineSegment(sketch, "E79.right", {"start": v(66.12, -3) * mm, "end": v(66.12, -5) * mm});
            skSolve(sketch);
        }
        {
            var Q0;
            Q0 = qSketchRegion(id + "F25", true);
            extrude(context, id + "F26", {"entities" : qUnion([Q0]), "operationType" : NewBodyOperationType.ADD, "depth" : 6 * mm});
        }
        {
            var Q0;
            Q0=makeQuery(id+"F1.opExtrude","SWEPT_FACE",FACE,{"disambiguationData":[OSD([sQuery(id+"F0.wireOp",EDGE,"E0.right")])]});
            cPlane(context, id + "F27", {"entities" : qUnion([Q0]), "cplaneType" : CPlaneType.OFFSET, "offset" : 1 * mm, "width" : 150 * mm, "height" : 150 * mm});
        }
        {
            var Q0;
            Q0=qCreatedBy(id+"F27.planeOp",FACE);
            var sketch = newSketch(context, id + "F28", { "sketchPlane" : qUnion([Q0])});
            skLineSegment(sketch, "E80.0", {"start": v(32.5, 0) * mm, "end": v(-32.5, 0) * mm, "construction": true});
            skLineSegment(sketch, "E81", {"start": v(-32.5, 0) * mm, "end": v(-32.5, -1) * mm, "construction": true});
            skLineSegment(sketch, "E82.bottom", {"start": v(-32.5, -1) * mm, "end": v(32.5, -1) * mm});
            skLineSegment(sketch, "E82.top", {"start": v(-32.5, 2) * mm, "end": v(32.5, 2) * mm});
            skLineSegment(sketch, "E82.left", {"start": v(-32.5, -1) * mm, "end": v(-32.5, 2) * mm});
            skLineSegment(sketch, "E82.right", {"start": v(32.5, -1) * mm, "end": v(32.5, 2) * mm});
            skLineSegment(sketch, "E83.bottom", {"start": v(-34.5, -8.75) * mm, "end": v(45.5, -8.75) * mm});
            skLineSegment(sketch, "E83.top", {"start": v(-34.5, 9.75) * mm, "end": v(45.5, 9.75) * mm});
            skLineSegment(sketch, "E83.left", {"start": v(-34.5, -8.75) * mm, "end": v(-34.5, 9.75) * mm});
            skLineSegment(sketch, "E83.right", {"start": v(45.5, -8.75) * mm, "end": v(45.5, 9.75) * mm});
            skLineSegment(sketch, "E84", {"start": v(32.5, 0.5) * mm, "end": v(45.5, 0.5) * mm, "construction": true});
            skSolve(sketch);
        }
        {
            var Q0;
            Q0 = qSketchRegion(id + "F28", true);
            extrude(context, id + "F29", {"entities" : qUnion([Q0]), "depth" : .5 * mm});
        }
        {
            var Q0;
            Q0=makeQuery(id+"F29.opExtrude","CAP_FACE",FACE,{"disambiguationData":[OSD([sQuery(id+"F28.wireOp",EDGE,"E82.bottom"),sQuery(id+"F28.wireOp",EDGE,"E82.top"),sQuery(id+"F28.wireOp",EDGE,"E82.left"),sQuery(id+"F28.wireOp",EDGE,"E82.right"),sQuery(id+"F28.wireOp",EDGE,"E83.bottom"),sQuery(id+"F28.wireOp",EDGE,"E83.top"),sQuery(id+"F28.wireOp",EDGE,"E83.left"),sQuery(id+"F28.wireOp",EDGE,"E83.right")])],"isStart":true});
            var sketch = newSketch(context, id + "F30", { "sketchPlane" : qUnion([Q0])});
            skLineSegment(sketch, "E85", {"start": v(-45.5, 0.5) * mm, "end": v(-33.5, 0.5) * mm, "construction": true});
            skLineSegment(sketch, "E86", {"start": v(-33.5, 9.75) * mm, "end": v(-37.04, 6.21) * mm});
            skLineSegment(sketch, "E87", {"start": v(-37.04, 6.21) * mm, "end": v(-45.5, 6.21) * mm});
            skLineSegment(sketch, "E88", {"start": v(-45.5, 6.21) * mm, "end": v(-45.5, 9.75) * mm});
            skLineSegment(sketch, "E89", {"start": v(-45.5, 9.75) * mm, "end": v(-33.5, 9.75) * mm});
            skLineSegment(sketch, "E90.MirrorCS", {"start": v(-33.5, -8.75) * mm, "end": v(-37.04, -5.21) * mm});
            skLineSegment(sketch, "E91.MirrorCS", {"start": v(-45.5, -8.75) * mm, "end": v(-33.5, -8.75) * mm});
            skLineSegment(sketch, "E92.MirrorCS", {"start": v(-37.04, -5.21) * mm, "end": v(-45.5, -5.21) * mm});
            skLineSegment(sketch, "E93.MirrorCS", {"start": v(-45.5, -5.21) * mm, "end": v(-45.5, -8.75) * mm});
            skSolve(sketch);
        }
        {
            var Q0;
            Q0 = qSketchRegion(id + "F30", true);
            extrude(context, id + "F31", {"entities" : qUnion([Q0]), "operationType" : NewBodyOperationType.REMOVE, "endBound" : BoundingType.THROUGH_ALL, "oppositeDirection" : true, "depth" : 25 * mm});
        }
        {
            var Q0;
            Q0=makeQuery(id+"F29.opExtrude","CAP_FACE",FACE,{"disambiguationData":[OSD([sQuery(id+"F28.wireOp",EDGE,"E82.bottom"),sQuery(id+"F28.wireOp",EDGE,"E82.top"),sQuery(id+"F28.wireOp",EDGE,"E82.left"),sQuery(id+"F28.wireOp",EDGE,"E82.right"),sQuery(id+"F28.wireOp",EDGE,"E83.bottom"),sQuery(id+"F28.wireOp",EDGE,"E83.top"),sQuery(id+"F28.wireOp",EDGE,"E83.left"),sQuery(id+"F28.wireOp",EDGE,"E83.right")])],"isStart":true});
            var sketch = newSketch(context, id + "F32", { "sketchPlane" : qUnion([Q0])});
            skLineSegment(sketch, "E94.0", {"start": v(-32, 0) * mm, "end": v(-27, 0) * mm, "construction": true});
            skLineSegment(sketch, "E95.0", {"start": v(32, 0) * mm, "end": v(27, 0) * mm, "construction": true});
            skLineSegment(sketch, "E96.bottom", {"start": v(33, -1) * mm, "end": v(26, -1) * mm});
            skLineSegment(sketch, "E96.top", {"start": v(33, -2) * mm, "end": v(26, -2) * mm});
            skLineSegment(sketch, "E96.left", {"start": v(33, -1) * mm, "end": v(33, -2) * mm});
            skLineSegment(sketch, "E96.right", {"start": v(26, -1) * mm, "end": v(26, -2) * mm});
            skLineSegment(sketch, "E97.top", {"start": v(-26, -2) * mm, "end": v(-33, -2) * mm});
            skLineSegment(sketch, "E97.left", {"start": v(-26, -1) * mm, "end": v(-26, -2) * mm});
            skLineSegment(sketch, "E97.right", {"start": v(-33, -1) * mm, "end": v(-33, -2) * mm});
            skLineSegment(sketch, "E98", {"start": v(-26, -1) * mm, "end": v(-33, -1) * mm});
            skLineSegment(sketch, "E99", {"start": v(-29.5, 0) * mm, "end": v(-29.5, -1) * mm, "construction": true});
            skLineSegment(sketch, "E100", {"start": v(29.5, 0) * mm, "end": v(29.5, -1) * mm, "construction": true});
            skSolve(sketch);
        }
        {
            var Q0;
            Q0 = qSketchRegion(id + "F32", true);
            extrude(context, id + "F33", {"entities" : qUnion([Q0]), "operationType" : NewBodyOperationType.ADD, "depth" : 10 * mm});
        }
        {
            var Q0;
            Q0=makeQuery(id+"F33.opExtrude","SWEPT_FACE",FACE,{"disambiguationData":[OSD([sQuery(id+"F32.wireOp",EDGE,"E96.top")])]});
            var sketch = newSketch(context, id + "F34", { "sketchPlane" : qUnion([Q0])});
            skCircle(sketch, "E101.0", {"center": v(-71, -29.5) * mm, "radius": 2.5 * mm});
            skCircle(sketch, "E102.0", {"center": v(-71, 29.5) * mm, "radius": 2.5 * mm});
            skSolve(sketch);
        }
        {
            var Q0;
            Q0 = qSketchRegion(id + "F34", true);
            extrude(context, id + "F35", {"entities" : qUnion([Q0]), "operationType" : NewBodyOperationType.REMOVE, "endBound" : BoundingType.UP_TO_NEXT, "oppositeDirection" : true, "depth" : 25 * mm});
        }
        {
            var Q0;
            Q0=makeQuery(id+"F29.opExtrude","CAP_FACE",FACE,{"disambiguationData":[OSD([sQuery(id+"F28.wireOp",EDGE,"E82.bottom"),sQuery(id+"F28.wireOp",EDGE,"E82.top"),sQuery(id+"F28.wireOp",EDGE,"E82.left"),sQuery(id+"F28.wireOp",EDGE,"E82.right"),sQuery(id+"F28.wireOp",EDGE,"E83.bottom"),sQuery(id+"F28.wireOp",EDGE,"E83.top"),sQuery(id+"F28.wireOp",EDGE,"E83.left"),sQuery(id+"F28.wireOp",EDGE,"E83.right")])],"isStart":false});
            var sketch = newSketch(context, id + "F36", { "sketchPlane" : qUnion([Q0])});
            skLineSegment(sketch, "E103.bottom", {"start": v(-34.5, -8.75) * mm, "end": v(-33.5, -8.75) * mm});
            skLineSegment(sketch, "E103.top", {"start": v(-34.5, 9.75) * mm, "end": v(-33.5, 9.75) * mm});
            skLineSegment(sketch, "E103.left", {"start": v(-34.5, -8.75) * mm, "end": v(-34.5, 9.75) * mm});
            skLineSegment(sketch, "E103.right", {"start": v(-33.5, -8.75) * mm, "end": v(-33.5, 9.75) * mm});
            skSolve(sketch);
        }
        {
            var Q0;
            Q0 = qSketchRegion(id + "F36", true);
            extrude(context, id + "F37", {"entities" : qUnion([Q0]), "operationType" : NewBodyOperationType.ADD, "depth" : 11 * mm});
        }
        {
            var Q0;
            Q0=makeQuery(id+"F37.boolean.opBoolean","MERGE",FACE,{"derivedFrom":[makeQuery(id+"F29.opExtrude","SWEPT_FACE",FACE,{"disambiguationData":[OSD([sQuery(id+"F28.wireOp",EDGE,"E83.left")])]}),makeQuery(id+"F37.opExtrude","SWEPT_FACE",FACE,{"disambiguationData":[OSD([sQuery(id+"F36.wireOp",EDGE,"E103.left")])]})]});
            var sketch = newSketch(context, id + "F38", { "sketchPlane" : qUnion([Q0])});
            skLineSegment(sketch, "E104", {"start": v(88.5, -8.75) * mm, "end": v(88.5, -3.75) * mm, "construction": true});
            skLineSegment(sketch, "E105.bottom", {"start": v(88.5, -3.75) * mm, "end": v(84.5, -3.75) * mm});
            skLineSegment(sketch, "E105.top", {"start": v(88.5, -0.75) * mm, "end": v(84.5, -0.75) * mm});
            skLineSegment(sketch, "E105.left", {"start": v(88.5, -3.75) * mm, "end": v(88.5, -0.75) * mm});
            skLineSegment(sketch, "E105.right", {"start": v(84.5, -3.75) * mm, "end": v(84.5, -0.75) * mm});
            skLineSegment(sketch, "E106.bottom", {"start": v(81, 9.75) * mm, "end": v(86, 9.75) * mm});
            skLineSegment(sketch, "E106.top", {"start": v(81, 2.75) * mm, "end": v(86, 2.75) * mm});
            skLineSegment(sketch, "E106.left", {"start": v(81, 9.75) * mm, "end": v(81, 2.75) * mm});
            skLineSegment(sketch, "E106.right", {"start": v(86, 9.75) * mm, "end": v(86, 2.75) * mm});
            skLineSegment(sketch, "E107", {"start": v(86, 9.75) * mm, "end": v(88.5, 9.75) * mm, "construction": true});
            skSolve(sketch);
        }
        {
            var Q0;
            Q0 = qSketchRegion(id + "F38", true);
            extrude(context, id + "F39", {"entities" : qUnion([Q0]), "operationType" : NewBodyOperationType.REMOVE, "endBound" : BoundingType.THROUGH_ALL, "oppositeDirection" : true, "depth" : 25 * mm});
        }
        {
            var Q0;
            Q0=makeQuery(id+"F39.boolean.opBoolean","COPY",EDGE,{"derivedFrom":makeQuery(id+"F39.opExtrude","SWEPT_EDGE",EDGE,{"disambiguationData":[OSD([sQuery(id+"F38.wireOp",EDGE,"E106.top"),sQuery(id+"F38.wireOp",EDGE,"E106.left")])]})});
            var Q1;
            Q1=makeQuery(id+"F39.boolean.opBoolean","COPY",EDGE,{"derivedFrom":makeQuery(id+"F39.opExtrude","SWEPT_EDGE",EDGE,{"disambiguationData":[OSD([sQuery(id+"F38.wireOp",EDGE,"E106.top"),sQuery(id+"F38.wireOp",EDGE,"E106.right")])]})});
            var Q2;
            Q2=makeQuery(id+"F33.opExtrude","CAP_EDGE",EDGE,{"disambiguationData":[OSD([sQuery(id+"F32.wireOp",EDGE,"E96.left")])],"isStart":false});
            var Q3;
            Q3=makeQuery(id+"F33.opExtrude","CAP_EDGE",EDGE,{"disambiguationData":[OSD([sQuery(id+"F32.wireOp",EDGE,"E96.right")])],"isStart":false});
            var Q4;
            Q4=makeQuery(id+"F33.opExtrude","CAP_EDGE",EDGE,{"disambiguationData":[OSD([sQuery(id+"F32.wireOp",EDGE,"E97.left")])],"isStart":false});
            var Q5;
            Q5=makeQuery(id+"F33.opExtrude","CAP_EDGE",EDGE,{"disambiguationData":[OSD([sQuery(id+"F32.wireOp",EDGE,"E97.right")])],"isStart":false});
            fillet(context, id + "F40", {"entities" : qUnion([Q0, Q1, Q2, Q3, Q4, Q5]), "radius" : 2 * mm, "tangentPropagation" : true, "allowEdgeOverflow" : false});
        }
        {
            var Q0;
            Q0=makeQuery(id+"F3.opExtrude","SWEPT_FACE",FACE,{"disambiguationData":[OSD([sQuery(id+"F2.wireOp",EDGE,"E21.top")])]});
            var sketch = newSketch(context, id + "F41", { "sketchPlane" : qUnion([Q0])});
            skLineSegment(sketch, "E108.bottom", {"start": v(-50, 2) * mm, "end": v(-41, 2) * mm});
            skLineSegment(sketch, "E108.top", {"start": v(-50, 2.1) * mm, "end": v(-41, 2.1) * mm});
            skLineSegment(sketch, "E108.left", {"start": v(-50, 2) * mm, "end": v(-50, 2.1) * mm});
            skLineSegment(sketch, "E108.right", {"start": v(-41, 2) * mm, "end": v(-41, 2.1) * mm});
            skSolve(sketch);
        }
        {
            var Q0;
            Q0 = qSketchRegion(id + "F41", true);
            extrude(context, id + "F42", {"entities" : qUnion([Q0]), "operationType" : NewBodyOperationType.REMOVE, "endBound" : BoundingType.THROUGH_ALL, "oppositeDirection" : true, "depth" : 25 * mm});
        }
        {
            var Q0;
            Q0=makeQuery(id+"F24.opExtrude","CAP_FACE",FACE,{"disambiguationData":[OSD([sQuery(id+"F23.wireOp",EDGE,"E77.bottom"),sQuery(id+"F23.wireOp",EDGE,"E77.top"),sQuery(id+"F23.wireOp",EDGE,"E77.left"),sQuery(id+"F23.wireOp",EDGE,"E77.right")])],"isStart":true});
            var Q1;
            {var subQ0=sQuery(id+"F0.wireOp",EDGE,"E8");var subQ1=sQuery(id+"F0.wireOp",EDGE,"E7");var subQ2=sQuery(id+"F0.wireOp",EDGE,"E6");var subQ3=sQuery(id+"F0.wireOp",EDGE,"E5");var subQ4=sQuery(id+"F0.wireOp",EDGE,"E4");var subQ5=sQuery(id+"F0.wireOp",EDGE,"E3");var subQ6=sQuery(id+"F0.wireOp",EDGE,"E2");var subQ7=sQuery(id+"F0.wireOp",EDGE,"E1");var subQ8=sQuery(id+"F6.wireOp",EDGE,"E36.bottom");var subQ9=makeQuery(id+"F7.opExtrude","SWEPT_FACE",FACE,{"disambiguationData":[OSD([subQ8])]});var subQ10=sQuery(id+"F4.wireOp",EDGE,"E31.bottom");var subQ11=makeQuery(id+"F5.opExtrude","SWEPT_FACE",FACE,{"disambiguationData":[OSD([subQ10])]});var subQ12=sQuery(id+"F0.wireOp",EDGE,"E20");var subQ13=sQuery(id+"F0.wireOp",EDGE,"E19.MirrorC");var subQ14=sQuery(id+"F0.wireOp",EDGE,"E17");var subQ15=sQuery(id+"F0.wireOp",EDGE,"E15");var subQ16=sQuery(id+"F0.wireOp",EDGE,"E14");var subQ17=sQuery(id+"F0.wireOp",EDGE,"E13");var subQ18=sQuery(id+"F0.wireOp",EDGE,"E12");var subQ19=sQuery(id+"F0.wireOp",EDGE,"E11");var subQ20=sQuery(id+"F0.wireOp",EDGE,"E10");var subQ21=sQuery(id+"F0.wireOp",EDGE,"E9");var subQ22=sQuery(id+"F0.wireOp",EDGE,"E0.right");var subQ23=sQuery(id+"F0.wireOp",EDGE,"E0.top");var subQ24=makeQuery(id+"F1.opExtrude","CAP_FACE",FACE,{"disambiguationData":[OSD([subQ23,subQ22,subQ7,subQ6,subQ5,subQ4,subQ3,subQ2,subQ1,subQ0,subQ21,subQ20,subQ19,subQ18,subQ17,subQ16,subQ15,subQ14,subQ13,subQ12])],"isStart":false});Q1=makeQuery(id+"F42.boolean.opBoolean","MERGE",FACE,{"derivedFrom":[makeQuery(id+"FQQAgOYBeqhCtfA_5.boolean.opBoolean","SPLIT",FACE,{"disambiguationData":[TD([makeQuery(id+"F1.opExtrude","SWEPT_FACE",FACE,{"disambiguationData":[OSD([subQ23])]})])],"derivedFrom":makeQuery(id+"F7.boolean.opBoolean","MERGE",FACE,{"derivedFrom":[makeQuery(id+"F5.boolean.opBoolean","MERGE",FACE,{"derivedFrom":[subQ24,subQ11]}),subQ9]})}),makeQuery(id+"F42.opExtrude","SWEPT_FACE",FACE,{"disambiguationData":[OSD([sQuery(id+"F41.wireOp",EDGE,"E108.bottom")])]})]});}
            extrude(context, id + "F43", {"entities" : qUnion([Q0]), "operationType" : NewBodyOperationType.ADD, "endBound" : BoundingType.UP_TO_SURFACE, "endBoundEntityFace" : qUnion([Q1]), "depth" : 25 * mm});
        }
        {
            var Q0;
            Q0=makeQuery(id+"F12.opExtrude","SWEPT_FACE",FACE,{"disambiguationData":[OSD([sQuery(id+"F11.wireOp",EDGE,"E44.top")])]});
            var sketch = newSketch(context, id + "F44", { "sketchPlane" : qUnion([Q0])});
            skLineSegment(sketch, "E109.bottom", {"start": v(60, 0) * mm, "end": v(51, 0) * mm});
            skLineSegment(sketch, "E109.top", {"start": v(60, -0.1) * mm, "end": v(51, -0.1) * mm});
            skLineSegment(sketch, "E109.left", {"start": v(60, 0) * mm, "end": v(60, -0.1) * mm});
            skLineSegment(sketch, "E109.right", {"start": v(51, 0) * mm, "end": v(51, -0.1) * mm});
            skSolve(sketch);
        }
        {
            var Q0;
            Q0 = qSketchRegion(id + "F44", true);
            extrude(context, id + "F45", {"entities" : qUnion([Q0]), "operationType" : NewBodyOperationType.REMOVE, "endBound" : BoundingType.THROUGH_ALL, "oppositeDirection" : true, "depth" : 25 * mm});
        }
        {
            var Q0;
            Q0=makeQuery(id+"F10.opExtrude","SWEPT_FACE",FACE,{"disambiguationData":[OSD([sQuery(id+"F9.wireOp",EDGE,"E38.2")])]});
            var sketch = newSketch(context, id + "F46", { "sketchPlane" : qUnion([Q0])});
            skPoint(sketch, "E110", {"position": v(11, 30.92) * mm});
            skPoint(sketch, "E111", {"position": v(11, 8.92) * mm});
            skSolve(sketch);
        }
        {
            var Q0;
            Q0=makeQuery(id+"F10.opExtrude","SWEPT_FACE",FACE,{"disambiguationData":[OSD([sQuery(id+"F9.wireOp",EDGE,"E38.3")])]});
            var sketch = newSketch(context, id + "F47", { "sketchPlane" : qUnion([Q0])});
            skPoint(sketch, "E112", {"position": v(-11, 2.5) * mm});
            skSolve(sketch);
        }
        {
            var Q0;
            Q0=makeQuery(id+"F10.opExtrude","SWEPT_EDGE",EDGE,{"disambiguationData":[OSD([sQuery(id+"F9.wireOp",EDGE,"E38.1"),sQuery(id+"F9.wireOp",EDGE,"E38.2")])]});
            cPoint(context, id + "F48", {"entities" : qUnion([Q0]), "parameter" : 0.5});
        }
        {
            var Q0;
            Q0=sQuery(id+"F47.wireOp",VERTEX,"E112");
            var Q1;
            Q1=sQuery(id+"F46.wireOp",VERTEX,"E110");
            var Q2;
            Q2 = qCreatedBy(id + "F48" ,VERTEX);
            cPlane(context, id + "F49", {"entities" : qUnion([Q0, Q1, Q2]), "cplaneType" : CPlaneType.THREE_POINT, "offset" : 25 * mm, "width" : 150 * mm, "height" : 150 * mm});
        }
        {
            var Q0;
            Q0=qCreatedBy(id+"F49.planeOp",FACE);
            var sketch = newSketch(context, id + "F50", { "sketchPlane" : qUnion([Q0])});
            skPoint(sketch, "E113.0", {"position": v(-8.92, 4.5) * mm});
            skPoint(sketch, "E114.0", {"position": v(-8.92, 2.5) * mm});
            skPoint(sketch, "E115.0", {"position": v(-1.08, 2.5) * mm});
            skPoint(sketch, "E116.0", {"position": v(-1.08, 4.5) * mm});
            skLineSegment(sketch, "E117", {"start": v(-8.92, 4.5) * mm, "end": v(-1.08, 4.5) * mm, "construction": true});
            skLineSegment(sketch, "E118", {"start": v(-8.92, 2.5) * mm, "end": v(-1.08, 2.5) * mm, "construction": true});
            skLineSegment(sketch, "E119", {"start": v(-5, 2.5) * mm, "end": v(-5, 4.5) * mm, "construction": true});
            skSolve(sketch);
        }
        {
            var Q0;
            Q0=makeQuery(id+"F10.opExtrude","SWEPT_BODY",BODY,{"disambiguationData":[OSD([sQuery(id+"F9.wireOp",EDGE,"E38.0"),sQuery(id+"F9.wireOp",EDGE,"E38.1"),sQuery(id+"F9.wireOp",EDGE,"E38.2"),sQuery(id+"F9.wireOp",EDGE,"E38.3")])]});
            var Q1;
            Q1=makeQuery(id+"F42.boolean.opBoolean","SPLIT",BODY,{"disambiguationData":[OD(2.0)],"derivedFrom":makeQuery(id+"F1.opExtrude","SWEPT_BODY",BODY,{"disambiguationData":[OSD([sQuery(id+"F0.wireOp",EDGE,"E0.top"),sQuery(id+"F0.wireOp",EDGE,"E0.right"),sQuery(id+"F0.wireOp",EDGE,"E1"),sQuery(id+"F0.wireOp",EDGE,"E2"),sQuery(id+"F0.wireOp",EDGE,"E3"),sQuery(id+"F0.wireOp",EDGE,"E4"),sQuery(id+"F0.wireOp",EDGE,"E5"),sQuery(id+"F0.wireOp",EDGE,"E6"),sQuery(id+"F0.wireOp",EDGE,"E7"),sQuery(id+"F0.wireOp",EDGE,"E8"),sQuery(id+"F0.wireOp",EDGE,"E9"),sQuery(id+"F0.wireOp",EDGE,"E10"),sQuery(id+"F0.wireOp",EDGE,"E11"),sQuery(id+"F0.wireOp",EDGE,"E12"),sQuery(id+"F0.wireOp",EDGE,"E13"),sQuery(id+"F0.wireOp",EDGE,"E14"),sQuery(id+"F0.wireOp",EDGE,"E15"),sQuery(id+"F0.wireOp",EDGE,"E17"),sQuery(id+"F0.wireOp",EDGE,"E19.MirrorC"),sQuery(id+"F0.wireOp",EDGE,"E20")])]})});
            var Q2;
            Q2=makeQuery(id+"F10.opExtrude","SWEPT_BODY",BODY,{"disambiguationData":[OSD([sQuery(id+"F9.wireOp",EDGE,"E39.0"),sQuery(id+"F9.wireOp",EDGE,"E39.1"),sQuery(id+"F9.wireOp",EDGE,"E39.2"),sQuery(id+"F9.wireOp",EDGE,"E39.3")])]});
            var Q3;
            Q3=makeQuery(id+"F42.boolean.opBoolean","SPLIT",BODY,{"disambiguationData":[OD(1.0)],"derivedFrom":makeQuery(id+"F1.opExtrude","SWEPT_BODY",BODY,{"disambiguationData":[OSD([sQuery(id+"F0.wireOp",EDGE,"E0.top"),sQuery(id+"F0.wireOp",EDGE,"E0.right"),sQuery(id+"F0.wireOp",EDGE,"E1"),sQuery(id+"F0.wireOp",EDGE,"E2"),sQuery(id+"F0.wireOp",EDGE,"E3"),sQuery(id+"F0.wireOp",EDGE,"E4"),sQuery(id+"F0.wireOp",EDGE,"E5"),sQuery(id+"F0.wireOp",EDGE,"E6"),sQuery(id+"F0.wireOp",EDGE,"E7"),sQuery(id+"F0.wireOp",EDGE,"E8"),sQuery(id+"F0.wireOp",EDGE,"E9"),sQuery(id+"F0.wireOp",EDGE,"E10"),sQuery(id+"F0.wireOp",EDGE,"E11"),sQuery(id+"F0.wireOp",EDGE,"E12"),sQuery(id+"F0.wireOp",EDGE,"E13"),sQuery(id+"F0.wireOp",EDGE,"E14"),sQuery(id+"F0.wireOp",EDGE,"E15"),sQuery(id+"F0.wireOp",EDGE,"E17"),sQuery(id+"F0.wireOp",EDGE,"E19.MirrorC"),sQuery(id+"F0.wireOp",EDGE,"E20")])]})});
            var Q4;
            Q4=sQuery(id+"F50.wireOp",EDGE,"E119");
            transform(context, id + "F51", {"entities" : qUnion([Q0, Q1, Q2, Q3]), "transformType" : TransformType.ROTATION, "transformAxis" : qUnion([Q4]), "angle" : 180 * degree, "makeCopy" : false});
        }
        {
            var Q0;
            Q0=makeQuery(id+"F10.opExtrude","SWEPT_FACE",FACE,{"disambiguationData":[OSD([sQuery(id+"F9.wireOp",EDGE,"E39.0")])]});
            var sketch = newSketch(context, id + "F52", { "sketchPlane" : qUnion([Q0])});
            skPoint(sketch, "E120", {"position": v(-44, 19.92) * mm});
            skLineSegment(sketch, "E121.0", {"start": v(-44, -20.92) * mm, "end": v(-44, 1.08) * mm, "construction": true});
            skPoint(sketch, "E122", {"position": v(-44, -9.92) * mm});
            skArc(sketch, "E123", {"start": v(-44, 17.42) * mm, "mid": v(-41.5, 19.92) * mm, "end": v(-44, 22.42) * mm});
            skArc(sketch, "E124", {"start": v(-44, -12.42) * mm, "mid": v(-41.5, -9.92) * mm, "end": v(-44, -7.42) * mm});
            skLineSegment(sketch, "E125", {"start": v(-44, 22.42) * mm, "end": v(-44, 17.42) * mm});
            skLineSegment(sketch, "E126", {"start": v(-44, -7.42) * mm, "end": v(-44, -12.42) * mm});
            skArc(sketch, "E127", {"start": v(-44, 22.42) * mm, "mid": v(-46.5, 19.92) * mm, "end": v(-44, 17.42) * mm});
            skArc(sketch, "E128", {"start": v(-44, -7.42) * mm, "mid": v(-46.5, -9.92) * mm, "end": v(-44, -12.42) * mm});
            skSolve(sketch);
        }
        {
            var Q0;
            Q0 = qSketchRegion(id + "F52", true);
            var Q1;
            Q1=makeQuery(id+"F45.boolean.opBoolean","MERGE",FACE,{"derivedFrom":[makeQuery(id+"F14.boolean.opBoolean","MERGE",FACE,{"derivedFrom":[makeQuery(id+"F1.opExtrude","CAP_FACE",FACE,{"disambiguationData":[OSD([sQuery(id+"F0.wireOp",EDGE,"E0.top"),sQuery(id+"F0.wireOp",EDGE,"E0.right"),sQuery(id+"F0.wireOp",EDGE,"E1"),sQuery(id+"F0.wireOp",EDGE,"E2"),sQuery(id+"F0.wireOp",EDGE,"E3"),sQuery(id+"F0.wireOp",EDGE,"E4"),sQuery(id+"F0.wireOp",EDGE,"E5"),sQuery(id+"F0.wireOp",EDGE,"E6"),sQuery(id+"F0.wireOp",EDGE,"E7"),sQuery(id+"F0.wireOp",EDGE,"E8"),sQuery(id+"F0.wireOp",EDGE,"E9"),sQuery(id+"F0.wireOp",EDGE,"E10"),sQuery(id+"F0.wireOp",EDGE,"E11"),sQuery(id+"F0.wireOp",EDGE,"E12"),sQuery(id+"F0.wireOp",EDGE,"E13"),sQuery(id+"F0.wireOp",EDGE,"E14"),sQuery(id+"F0.wireOp",EDGE,"E15"),sQuery(id+"F0.wireOp",EDGE,"E17"),sQuery(id+"F0.wireOp",EDGE,"E19.MirrorC"),sQuery(id+"F0.wireOp",EDGE,"E20")])],"isStart":true}),makeQuery(id+"F14.opExtrude","SWEPT_FACE",FACE,{"disambiguationData":[OSD([sQuery(id+"F13.wireOp",EDGE,"E58.bottom")])]}),makeQuery(id+"F14.opExtrude","SWEPT_FACE",FACE,{"disambiguationData":[OSD([sQuery(id+"F13.wireOp",EDGE,"E63.MirrorCS")])]})]}),makeQuery(id+"F45.opExtrude","SWEPT_FACE",FACE,{"disambiguationData":[OSD([sQuery(id+"F44.wireOp",EDGE,"E109.bottom")])]})]});
            extrude(context, id + "F53", {"entities" : qUnion([Q0]), "operationType" : NewBodyOperationType.REMOVE, "endBound" : BoundingType.UP_TO_SURFACE, "oppositeDirection" : true, "endBoundEntityFace" : qUnion([Q1]), "depth" : 25 * mm});
        }
        {
            var Q0;
            Q0=makeQuery(id+"F29.opExtrude","CAP_FACE",FACE,{"disambiguationData":[OSD([sQuery(id+"F28.wireOp",EDGE,"E82.bottom"),sQuery(id+"F28.wireOp",EDGE,"E82.top"),sQuery(id+"F28.wireOp",EDGE,"E82.left"),sQuery(id+"F28.wireOp",EDGE,"E82.right"),sQuery(id+"F28.wireOp",EDGE,"E83.bottom"),sQuery(id+"F28.wireOp",EDGE,"E83.top"),sQuery(id+"F28.wireOp",EDGE,"E83.left"),sQuery(id+"F28.wireOp",EDGE,"E83.right")])],"isStart":false});
            var sketch = newSketch(context, id + "F54", { "sketchPlane" : qUnion([Q0])});
            skLineSegment(sketch, "E129.bottom", {"start": v(-29.47, 8.38) * mm, "end": v(-24.47, 8.38) * mm});
            skLineSegment(sketch, "E129.top", {"start": v(-29.47, 3.38) * mm, "end": v(-24.47, 3.38) * mm});
            skLineSegment(sketch, "E129.left", {"start": v(-29.47, 8.38) * mm, "end": v(-29.47, 3.38) * mm});
            skLineSegment(sketch, "E129.right", {"start": v(-24.47, 8.38) * mm, "end": v(-24.47, 3.38) * mm});
            skLineSegment(sketch, "E130", {"start": v(-32.5, 0.5) * mm, "end": v(32.5, 0.5) * mm, "construction": true});
            skLineSegment(sketch, "E131", {"start": v(-24.47, 9.75) * mm, "end": v(-24.47, 2) * mm, "construction": true});
            skPoint(sketch, "E132", {"position": v(-24.47, 5.88) * mm});
            skLineSegment(sketch, "E133.1.0.0", {"start": v(-22.47, 3.38) * mm, "end": v(-17.47, 3.38) * mm});
            skLineSegment(sketch, "E133.1.0.1", {"start": v(-22.47, 8.38) * mm, "end": v(-22.47, 3.38) * mm});
            skLineSegment(sketch, "E133.1.0.2", {"start": v(-22.47, 8.38) * mm, "end": v(-17.47, 8.38) * mm});
            skLineSegment(sketch, "E133.1.0.3", {"start": v(-17.47, 8.38) * mm, "end": v(-17.47, 3.38) * mm});
            skLineSegment(sketch, "E133.2.0.0", {"start": v(-15.47, 3.38) * mm, "end": v(-10.47, 3.38) * mm});
            skLineSegment(sketch, "E133.2.0.1", {"start": v(-15.47, 8.38) * mm, "end": v(-15.47, 3.38) * mm});
            skLineSegment(sketch, "E133.2.0.2", {"start": v(-15.47, 8.38) * mm, "end": v(-10.47, 8.38) * mm});
            skLineSegment(sketch, "E133.2.0.3", {"start": v(-10.47, 8.38) * mm, "end": v(-10.47, 3.38) * mm});
            skLineSegment(sketch, "E133.3.0.0", {"start": v(-8.47, 3.38) * mm, "end": v(-3.47, 3.38) * mm});
            skLineSegment(sketch, "E133.3.0.1", {"start": v(-8.47, 8.38) * mm, "end": v(-8.47, 3.38) * mm});
            skLineSegment(sketch, "E133.3.0.2", {"start": v(-8.47, 8.38) * mm, "end": v(-3.47, 8.38) * mm});
            skLineSegment(sketch, "E133.3.0.3", {"start": v(-3.47, 8.38) * mm, "end": v(-3.47, 3.38) * mm});
            skLineSegment(sketch, "E133.4.0.0", {"start": v(-1.47, 3.38) * mm, "end": v(3.53, 3.38) * mm});
            skLineSegment(sketch, "E133.4.0.1", {"start": v(-1.47, 8.38) * mm, "end": v(-1.47, 3.38) * mm});
            skLineSegment(sketch, "E133.4.0.2", {"start": v(-1.47, 8.38) * mm, "end": v(3.53, 8.38) * mm});
            skLineSegment(sketch, "E133.4.0.3", {"start": v(3.53, 8.38) * mm, "end": v(3.53, 3.38) * mm});
            skLineSegment(sketch, "E133.5.0.0", {"start": v(5.53, 3.38) * mm, "end": v(10.53, 3.38) * mm});
            skLineSegment(sketch, "E133.5.0.1", {"start": v(5.53, 8.38) * mm, "end": v(5.53, 3.38) * mm});
            skLineSegment(sketch, "E133.5.0.2", {"start": v(5.53, 8.38) * mm, "end": v(10.53, 8.38) * mm});
            skLineSegment(sketch, "E133.5.0.3", {"start": v(10.53, 8.38) * mm, "end": v(10.53, 3.38) * mm});
            skLineSegment(sketch, "E133.6.0.0", {"start": v(12.53, 3.38) * mm, "end": v(17.53, 3.38) * mm});
            skLineSegment(sketch, "E133.6.0.1", {"start": v(12.53, 8.38) * mm, "end": v(12.53, 3.38) * mm});
            skLineSegment(sketch, "E133.6.0.2", {"start": v(12.53, 8.38) * mm, "end": v(17.53, 8.38) * mm});
            skLineSegment(sketch, "E133.6.0.3", {"start": v(17.53, 8.38) * mm, "end": v(17.53, 3.38) * mm});
            skLineSegment(sketch, "E133.7.0.0", {"start": v(19.53, 3.38) * mm, "end": v(24.53, 3.38) * mm});
            skLineSegment(sketch, "E133.7.0.1", {"start": v(19.53, 8.38) * mm, "end": v(19.53, 3.38) * mm});
            skLineSegment(sketch, "E133.7.0.2", {"start": v(19.53, 8.38) * mm, "end": v(24.53, 8.38) * mm});
            skLineSegment(sketch, "E133.7.0.3", {"start": v(24.53, 8.38) * mm, "end": v(24.53, 3.38) * mm});
            skLineSegment(sketch, "E133.8.0.0", {"start": v(26.53, 3.38) * mm, "end": v(31.53, 3.38) * mm});
            skLineSegment(sketch, "E133.8.0.1", {"start": v(26.53, 8.38) * mm, "end": v(26.53, 3.38) * mm});
            skLineSegment(sketch, "E133.8.0.2", {"start": v(26.53, 8.38) * mm, "end": v(31.53, 8.38) * mm});
            skLineSegment(sketch, "E133.8.0.3", {"start": v(31.53, 8.38) * mm, "end": v(31.53, 3.38) * mm});
            skLineSegment(sketch, "E133.direction1", {"start": v(-29.47, 3.38) * mm, "end": v(-22.47, 3.38) * mm, "construction": true});
            skLineSegment(sketch, "E134.MirrorCS", {"start": v(-29.47, -2.38) * mm, "end": v(-24.47, -2.38) * mm});
            skLineSegment(sketch, "E135.MirrorCS", {"start": v(19.53, -7.38) * mm, "end": v(24.53, -7.38) * mm});
            skLineSegment(sketch, "E136.MirrorCS", {"start": v(-8.47, -7.38) * mm, "end": v(-3.47, -7.38) * mm});
            skLineSegment(sketch, "E137.MirrorCS", {"start": v(12.53, -7.38) * mm, "end": v(12.53, -2.38) * mm});
            skLineSegment(sketch, "E138.MirrorCS", {"start": v(5.53, -7.38) * mm, "end": v(5.53, -2.38) * mm});
            skLineSegment(sketch, "E139.MirrorCS", {"start": v(17.53, -7.38) * mm, "end": v(17.53, -2.38) * mm});
            skLineSegment(sketch, "E140.MirrorCS", {"start": v(26.53, -7.38) * mm, "end": v(31.53, -7.38) * mm});
            skLineSegment(sketch, "E141.MirrorCS", {"start": v(-1.47, -7.38) * mm, "end": v(3.53, -7.38) * mm});
            skLineSegment(sketch, "E142.MirrorCS", {"start": v(12.53, -2.38) * mm, "end": v(17.53, -2.38) * mm});
            skLineSegment(sketch, "E143.MirrorCS", {"start": v(-29.47, -7.38) * mm, "end": v(-29.47, -2.38) * mm});
            skLineSegment(sketch, "E144.MirrorCS", {"start": v(-24.47, -7.38) * mm, "end": v(-24.47, -2.38) * mm});
            skLineSegment(sketch, "E145.MirrorCS", {"start": v(-22.47, -2.38) * mm, "end": v(-17.47, -2.38) * mm});
            skLineSegment(sketch, "E146.MirrorCS", {"start": v(-10.47, -7.38) * mm, "end": v(-10.47, -2.38) * mm});
            skLineSegment(sketch, "E147.MirrorCS", {"start": v(-8.47, -7.38) * mm, "end": v(-8.47, -2.38) * mm});
            skLineSegment(sketch, "E148.MirrorCS", {"start": v(-8.47, -2.38) * mm, "end": v(-3.47, -2.38) * mm});
            skLineSegment(sketch, "E149.MirrorCS", {"start": v(-29.47, -7.38) * mm, "end": v(-24.47, -7.38) * mm});
            skLineSegment(sketch, "E150.MirrorCS", {"start": v(26.53, -7.38) * mm, "end": v(26.53, -2.38) * mm});
            skLineSegment(sketch, "E151.MirrorCS", {"start": v(-1.47, -7.38) * mm, "end": v(-1.47, -2.38) * mm});
            skLineSegment(sketch, "E152.MirrorCS", {"start": v(10.53, -7.38) * mm, "end": v(10.53, -2.38) * mm});
            skLineSegment(sketch, "E153.MirrorCS", {"start": v(-22.47, -7.38) * mm, "end": v(-17.47, -7.38) * mm});
            skLineSegment(sketch, "E154.MirrorCS", {"start": v(-22.47, -7.38) * mm, "end": v(-22.47, -2.38) * mm});
            skLineSegment(sketch, "E155.MirrorCS", {"start": v(-15.47, -2.38) * mm, "end": v(-10.47, -2.38) * mm});
            skLineSegment(sketch, "E156.MirrorCS", {"start": v(-17.47, -7.38) * mm, "end": v(-17.47, -2.38) * mm});
            skLineSegment(sketch, "E157.MirrorCS", {"start": v(-15.47, -7.38) * mm, "end": v(-10.47, -7.38) * mm});
            skLineSegment(sketch, "E158.MirrorCS", {"start": v(-15.47, -7.38) * mm, "end": v(-15.47, -2.38) * mm});
            skLineSegment(sketch, "E159.MirrorCS", {"start": v(-29.47, -2.38) * mm, "end": v(-22.47, -2.38) * mm, "construction": true});
            skLineSegment(sketch, "E160.MirrorCS", {"start": v(19.53, -7.38) * mm, "end": v(19.53, -2.38) * mm});
            skLineSegment(sketch, "E161.MirrorCS", {"start": v(5.53, -2.38) * mm, "end": v(10.53, -2.38) * mm});
            skLineSegment(sketch, "E162.MirrorCS", {"start": v(26.53, -2.38) * mm, "end": v(31.53, -2.38) * mm});
            skLineSegment(sketch, "E163.MirrorCS", {"start": v(-1.47, -2.38) * mm, "end": v(3.53, -2.38) * mm});
            skLineSegment(sketch, "E164.MirrorCS", {"start": v(24.53, -7.38) * mm, "end": v(24.53, -2.38) * mm});
            skLineSegment(sketch, "E165.MirrorCS", {"start": v(-3.47, -7.38) * mm, "end": v(-3.47, -2.38) * mm});
            skLineSegment(sketch, "E166.MirrorCS", {"start": v(5.53, -7.38) * mm, "end": v(10.53, -7.38) * mm});
            skLineSegment(sketch, "E167.MirrorCS", {"start": v(19.53, -2.38) * mm, "end": v(24.53, -2.38) * mm});
            skLineSegment(sketch, "E168.MirrorCS", {"start": v(12.53, -7.38) * mm, "end": v(17.53, -7.38) * mm});
            skPoint(sketch, "E169.MirrorP", {"position": v(-24.47, -4.88) * mm});
            skLineSegment(sketch, "E170.MirrorCS", {"start": v(31.53, -7.38) * mm, "end": v(31.53, -2.38) * mm});
            skLineSegment(sketch, "E171.MirrorCS", {"start": v(3.53, -7.38) * mm, "end": v(3.53, -2.38) * mm});
            skSolve(sketch);
        }
        {
            var Q0;
            Q0 = qSketchRegion(id + "F54", true);
            var Q1;
            Q1=makeQuery(id+"F29.opExtrude","CAP_FACE",FACE,{"disambiguationData":[OSD([sQuery(id+"F28.wireOp",EDGE,"E82.bottom"),sQuery(id+"F28.wireOp",EDGE,"E82.top"),sQuery(id+"F28.wireOp",EDGE,"E82.left"),sQuery(id+"F28.wireOp",EDGE,"E82.right"),sQuery(id+"F28.wireOp",EDGE,"E83.bottom"),sQuery(id+"F28.wireOp",EDGE,"E83.top"),sQuery(id+"F28.wireOp",EDGE,"E83.left"),sQuery(id+"F28.wireOp",EDGE,"E83.right")])],"isStart":true});
            extrude(context, id + "F55", {"entities" : qUnion([Q0]), "operationType" : NewBodyOperationType.REMOVE, "endBound" : BoundingType.UP_TO_SURFACE, "oppositeDirection" : true, "endBoundEntityFace" : qUnion([Q1]), "depth" : 25 * mm});
        }
        {
            var Q0;
            Q0=makeQuery(id+"F10.opExtrude","SWEPT_FACE",FACE,{"disambiguationData":[OSD([sQuery(id+"F9.wireOp",EDGE,"E39.0")])]});
            var sketch = newSketch(context, id + "F56", { "sketchPlane" : qUnion([Q0])});
            skLineSegment(sketch, "E172.bottom", {"start": v(-35.62, 26.8) * mm, "end": v(-16.88, 26.8) * mm});
            skLineSegment(sketch, "E172.top", {"start": v(-35.62, 12.48) * mm, "end": v(-16.88, 12.48) * mm});
            skLineSegment(sketch, "E172.left", {"start": v(-35.62, 26.8) * mm, "end": v(-35.62, 12.48) * mm});
            skLineSegment(sketch, "E172.right", {"start": v(-16.88, 26.8) * mm, "end": v(-16.88, 12.48) * mm});
            skLineSegment(sketch, "E173.1.0.0", {"start": v(-13.62, 26.8) * mm, "end": v(5.12, 26.8) * mm});
            skLineSegment(sketch, "E173.1.0.1", {"start": v(-13.62, 26.8) * mm, "end": v(-13.62, 12.48) * mm});
            skLineSegment(sketch, "E173.1.0.2", {"start": v(5.12, 26.8) * mm, "end": v(5.12, 12.48) * mm});
            skLineSegment(sketch, "E173.1.0.3", {"start": v(-13.62, 12.48) * mm, "end": v(5.12, 12.48) * mm});
            skLineSegment(sketch, "E173.2.0.0", {"start": v(8.38, 26.8) * mm, "end": v(27.12, 26.8) * mm});
            skLineSegment(sketch, "E173.2.0.1", {"start": v(8.38, 26.8) * mm, "end": v(8.38, 12.48) * mm});
            skLineSegment(sketch, "E173.2.0.2", {"start": v(27.12, 26.8) * mm, "end": v(27.12, 12.48) * mm});
            skLineSegment(sketch, "E173.2.0.3", {"start": v(8.38, 12.48) * mm, "end": v(27.12, 12.48) * mm});
            skLineSegment(sketch, "E173.3.0.0", {"start": v(30.38, 26.8) * mm, "end": v(49.12, 26.8) * mm});
            skLineSegment(sketch, "E173.3.0.1", {"start": v(30.38, 26.8) * mm, "end": v(30.38, 12.48) * mm});
            skLineSegment(sketch, "E173.3.0.2", {"start": v(49.12, 26.8) * mm, "end": v(49.12, 12.48) * mm});
            skLineSegment(sketch, "E173.3.0.3", {"start": v(30.38, 12.48) * mm, "end": v(49.12, 12.48) * mm});
            skLineSegment(sketch, "E173.direction1", {"start": v(-35.62, 26.8) * mm, "end": v(-13.62, 26.8) * mm, "construction": true});
            skLineSegment(sketch, "E174.0", {"start": v(11, 8.92) * mm, "end": v(11, 1.08) * mm, "construction": true});
            skPoint(sketch, "E175.0", {"position": v(11, 5) * mm});
            skLineSegment(sketch, "E176", {"start": v(4.3, 5) * mm, "end": v(16.8, 5) * mm, "construction": true});
            skLineSegment(sketch, "E177.MirrorCS", {"start": v(-35.62, -16.8) * mm, "end": v(-35.62, -2.48) * mm});
            skLineSegment(sketch, "E178.MirrorCS", {"start": v(-35.62, -16.8) * mm, "end": v(-16.88, -16.8) * mm});
            skLineSegment(sketch, "E179.MirrorCS", {"start": v(-35.62, -2.48) * mm, "end": v(-16.88, -2.48) * mm});
            skLineSegment(sketch, "E180.MirrorCS", {"start": v(-13.62, -16.8) * mm, "end": v(5.12, -16.8) * mm});
            skLineSegment(sketch, "E181.MirrorCS", {"start": v(-13.62, -16.8) * mm, "end": v(-13.62, -2.48) * mm});
            skLineSegment(sketch, "E182.MirrorCS", {"start": v(-13.62, -2.48) * mm, "end": v(5.12, -2.48) * mm});
            skLineSegment(sketch, "E183.MirrorCS", {"start": v(5.12, -16.8) * mm, "end": v(5.12, -2.48) * mm});
            skLineSegment(sketch, "E184.MirrorCS", {"start": v(8.38, -16.8) * mm, "end": v(8.38, -2.48) * mm});
            skLineSegment(sketch, "E185.MirrorCS", {"start": v(8.38, -16.8) * mm, "end": v(27.12, -16.8) * mm});
            skLineSegment(sketch, "E186.MirrorCS", {"start": v(8.38, -2.48) * mm, "end": v(27.12, -2.48) * mm});
            skLineSegment(sketch, "E187.MirrorCS", {"start": v(27.12, -16.8) * mm, "end": v(27.12, -2.48) * mm});
            skLineSegment(sketch, "E188.MirrorCS", {"start": v(30.38, -2.48) * mm, "end": v(49.12, -2.48) * mm});
            skLineSegment(sketch, "E189.MirrorCS", {"start": v(30.38, -16.8) * mm, "end": v(30.38, -2.48) * mm});
            skLineSegment(sketch, "E190.MirrorCS", {"start": v(30.38, -16.8) * mm, "end": v(49.12, -16.8) * mm});
            skLineSegment(sketch, "E191.MirrorCS", {"start": v(49.12, -16.8) * mm, "end": v(49.12, -2.48) * mm});
            skLineSegment(sketch, "E192.MirrorCS", {"start": v(-16.88, -16.8) * mm, "end": v(-16.88, -2.48) * mm});
            skSolve(sketch);
        }
        {
            var Q0;
            Q0 = qSketchRegion(id + "F56", true);
            extrude(context, id + "F57", {"entities" : qUnion([Q0]), "operationType" : NewBodyOperationType.ADD, "depth" : 1.35 * mm});
        }
        {
            var Q0;
            Q0=makeQuery(id+"F57.opExtrude","SWEPT_FACE",FACE,{"disambiguationData":[OSD([sQuery(id+"F56.wireOp",EDGE,"E178.MirrorCS")])]});
            var sketch = newSketch(context, id + "F58", { "sketchPlane" : qUnion([Q0])});
            skPoint(sketch, "E193.oppositeSnap0", {"position": v(-35.62, 4.6) * mm});
            skLineSegment(sketch, "E193.bottom", {"start": v(-35.62, 4.5) * mm, "end": v(49.31, 4.5) * mm});
            skLineSegment(sketch, "E193.top", {"start": v(-35.62, 4.6) * mm, "end": v(49.31, 4.6) * mm});
            skLineSegment(sketch, "E193.left", {"start": v(-35.62, 4.5) * mm, "end": v(-35.62, 4.6) * mm});
            skLineSegment(sketch, "E193.right", {"start": v(49.31, 4.5) * mm, "end": v(49.31, 4.6) * mm});
            skSolve(sketch);
        }
        {
            var Q0;
            Q0 = qSketchRegion(id + "F58", true);
            extrude(context, id + "F59", {"entities" : qUnion([Q0]), "operationType" : NewBodyOperationType.REMOVE, "endBound" : BoundingType.THROUGH_ALL, "oppositeDirection" : true, "depth" : 25 * mm});
        }
        {
            var Q0;
            Q0=makeQuery(id+"F1.opExtrude","SWEPT_EDGE",EDGE,{"disambiguationData":[OSD([sQuery(id+"F0.wireOp",EDGE,"E0.top"),sQuery(id+"F0.wireOp",EDGE,"E15")])]});
            var Q1;
            Q1=makeQuery(id+"F1.opExtrude","SWEPT_EDGE",EDGE,{"disambiguationData":[OSD([sQuery(id+"F0.wireOp",EDGE,"E15"),sQuery(id+"F0.wireOp",EDGE,"E20")])]});
            fillet(context, id + "F60", {"entities" : qUnion([Q0, Q1]), "radius" : 2 * mm, "tangentPropagation" : true, "allowEdgeOverflow" : false});
        }
        {
            var Q0;
            Q0=makeQuery(id+"F17.opExtrude","SWEPT_FACE",FACE,{"disambiguationData":[OSD([sQuery(id+"F16.wireOp",EDGE,"E66.0")])]});
            cPlane(context, id + "F61", {"entities" : qUnion([Q0]), "cplaneType" : CPlaneType.OFFSET, "offset" : .1 * mm, "width" : 150 * mm, "height" : 150 * mm});
        }
        {
            var Q0;
            Q0=qCreatedBy(id+"F61.planeOp",FACE);
            var sketch = newSketch(context, id + "F62", { "sketchPlane" : qUnion([Q0])});
            skLineSegment(sketch, "E194.0", {"start": v(49.12, -26.8) * mm, "end": v(49.12, -12.48) * mm});
            skLineSegment(sketch, "E195.0", {"start": v(30.38, -26.8) * mm, "end": v(49.12, -26.8) * mm});
            skLineSegment(sketch, "E196.0", {"start": v(30.38, -12.48) * mm, "end": v(49.12, -12.48) * mm});
            skLineSegment(sketch, "E197.0", {"start": v(30.38, -26.8) * mm, "end": v(30.38, -12.48) * mm});
            skLineSegment(sketch, "E198.0", {"start": v(27.12, 16.8) * mm, "end": v(27.12, 2.48) * mm});
            skLineSegment(sketch, "E198.1", {"start": v(-16.88, 16.8) * mm, "end": v(-16.88, 2.48) * mm});
            skLineSegment(sketch, "E198.2", {"start": v(-35.62, 16.8) * mm, "end": v(-35.62, 2.48) * mm});
            skLineSegment(sketch, "E198.3", {"start": v(30.38, 16.8) * mm, "end": v(49.12, 16.8) * mm});
            skLineSegment(sketch, "E198.4", {"start": v(49.12, 16.8) * mm, "end": v(49.12, 2.48) * mm});
            skLineSegment(sketch, "E198.5", {"start": v(30.38, 16.8) * mm, "end": v(30.38, 2.48) * mm});
            skLineSegment(sketch, "E198.6", {"start": v(30.38, 2.48) * mm, "end": v(49.12, 2.48) * mm});
            skLineSegment(sketch, "E198.7", {"start": v(5.12, 16.8) * mm, "end": v(5.12, 2.48) * mm});
            skLineSegment(sketch, "E198.8", {"start": v(8.38, 16.8) * mm, "end": v(8.38, 2.48) * mm});
            skLineSegment(sketch, "E198.9", {"start": v(-13.62, 16.8) * mm, "end": v(-13.62, 2.48) * mm});
            skLineSegment(sketch, "E198.10", {"start": v(-13.62, 2.48) * mm, "end": v(5.12, 2.48) * mm});
            skLineSegment(sketch, "E198.11", {"start": v(-35.62, 16.8) * mm, "end": v(-16.88, 16.8) * mm});
            skLineSegment(sketch, "E198.12", {"start": v(-35.62, 2.48) * mm, "end": v(-16.88, 2.48) * mm});
            skLineSegment(sketch, "E198.13", {"start": v(8.38, 16.8) * mm, "end": v(27.12, 16.8) * mm});
            skLineSegment(sketch, "E198.14", {"start": v(8.38, 2.48) * mm, "end": v(27.12, 2.48) * mm});
            skLineSegment(sketch, "E198.15", {"start": v(-13.62, 16.8) * mm, "end": v(5.12, 16.8) * mm});
            skLineSegment(sketch, "E198.16", {"start": v(49.12, 2.48) * mm, "end": v(30.38, 2.48) * mm});
            skLineSegment(sketch, "E198.17", {"start": v(30.38, 16.8) * mm, "end": v(49.12, 16.8) * mm});
            skLineSegment(sketch, "E198.18", {"start": v(27.12, 2.48) * mm, "end": v(8.38, 2.48) * mm});
            skLineSegment(sketch, "E198.19", {"start": v(8.38, 16.8) * mm, "end": v(27.12, 16.8) * mm});
            skLineSegment(sketch, "E198.20", {"start": v(-16.88, 2.48) * mm, "end": v(-35.62, 2.48) * mm});
            skLineSegment(sketch, "E198.21", {"start": v(-35.62, 16.8) * mm, "end": v(-16.88, 16.8) * mm});
            skLineSegment(sketch, "E198.22", {"start": v(5.12, 2.48) * mm, "end": v(-13.62, 2.48) * mm});
            skLineSegment(sketch, "E198.23", {"start": v(-13.62, 16.8) * mm, "end": v(5.12, 16.8) * mm});
            skLineSegment(sketch, "E199.0", {"start": v(8.38, -12.48) * mm, "end": v(27.12, -12.48) * mm});
            skLineSegment(sketch, "E199.1", {"start": v(8.38, -26.8) * mm, "end": v(27.12, -26.8) * mm});
            skLineSegment(sketch, "E199.2", {"start": v(8.38, -26.8) * mm, "end": v(8.38, -12.48) * mm});
            skLineSegment(sketch, "E199.3", {"start": v(-13.62, -12.48) * mm, "end": v(5.12, -12.48) * mm});
            skLineSegment(sketch, "E199.4", {"start": v(-35.62, -26.8) * mm, "end": v(-35.62, -12.48) * mm});
            skLineSegment(sketch, "E199.5", {"start": v(-16.88, -26.8) * mm, "end": v(-16.88, -12.48) * mm});
            skLineSegment(sketch, "E199.6", {"start": v(-35.62, -26.8) * mm, "end": v(-16.88, -26.8) * mm});
            skLineSegment(sketch, "E199.7", {"start": v(-35.62, -12.48) * mm, "end": v(-16.88, -12.48) * mm});
            skLineSegment(sketch, "E199.8", {"start": v(27.12, -26.8) * mm, "end": v(27.12, -12.48) * mm});
            skLineSegment(sketch, "E199.9", {"start": v(-13.62, -26.8) * mm, "end": v(-13.62, -12.48) * mm});
            skLineSegment(sketch, "E199.10", {"start": v(-13.62, -26.8) * mm, "end": v(5.12, -26.8) * mm});
            skLineSegment(sketch, "E199.11", {"start": v(5.12, -26.8) * mm, "end": v(5.12, -12.48) * mm});
            skLineSegment(sketch, "E199.13", {"start": v(27.12, -26.8) * mm, "end": v(8.38, -26.8) * mm});
            skLineSegment(sketch, "E199.14", {"start": v(-16.88, -12.48) * mm, "end": v(-16.88, -26.8) * mm});
            skLineSegment(sketch, "E199.15", {"start": v(-35.62, -26.8) * mm, "end": v(-35.62, -12.48) * mm});
            skLineSegment(sketch, "E199.16", {"start": v(5.12, -26.8) * mm, "end": v(-13.62, -26.8) * mm});
            skSolve(sketch);
        }
        {
            var Q0;
            Q0 = qSketchRegion(id + "F62", true);
            extrude(context, id + "F63", {"entities" : qUnion([Q0]), "depth" : 1.35 * mm});
        }
    });
